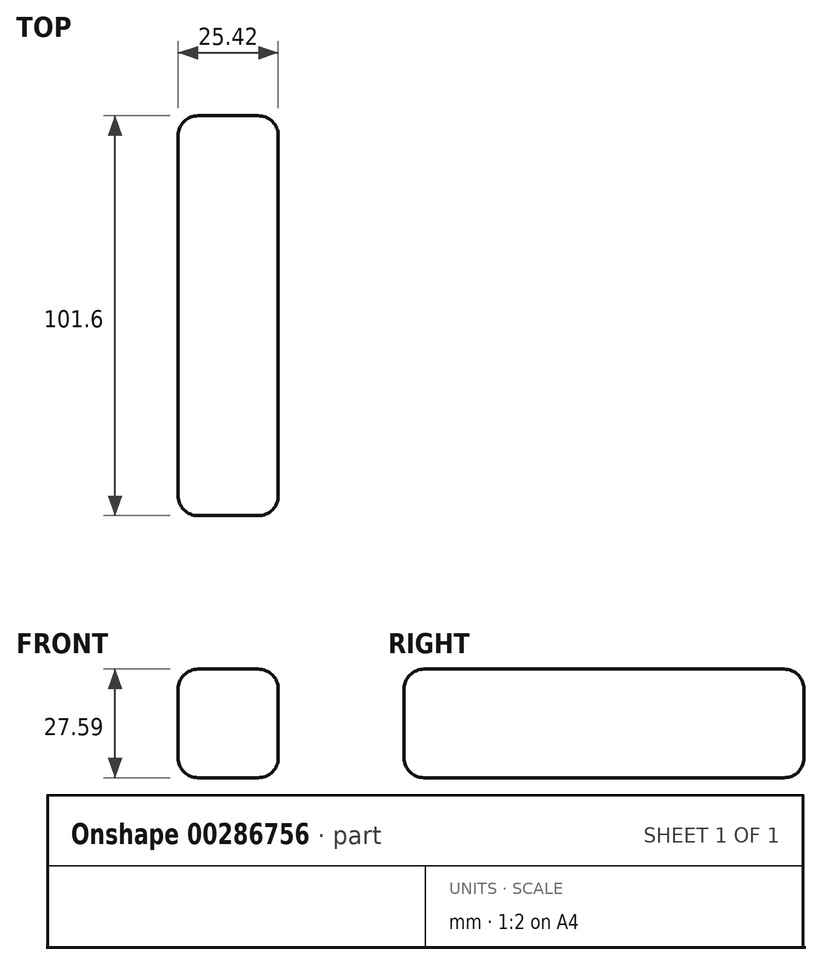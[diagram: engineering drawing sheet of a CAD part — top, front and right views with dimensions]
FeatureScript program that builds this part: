
annotation { "Feature Type Name" : "Feature", "Feature Type Description" : "" }
export const myFeature = defineFeature(function(context is Context, id is Id, definition is map)
    precondition{}
    {
        {
            var Q0;
            Q0=qCreatedBy(makeId("Front.planeOp"),FACE);
            var sketch = newSketch(context, id + "F0", { "sketchPlane" : qUnion([Q0])});
            skLineSegment(sketch, "E0.bottom", {"start": v(-37.05, 48.87) * mm, "end": v(-11.63, 48.87) * mm});
            skLineSegment(sketch, "E0.top", {"start": v(-37.05, 21.28) * mm, "end": v(-11.63, 21.28) * mm});
            skLineSegment(sketch, "E0.left", {"start": v(-37.05, 48.87) * mm, "end": v(-37.05, 21.28) * mm});
            skLineSegment(sketch, "E0.right", {"start": v(-11.63, 48.87) * mm, "end": v(-11.63, 21.28) * mm});
            skSolve(sketch);
        }
        {
            var Q0;
            Q0=makeQuery(id+"F0.imprint","IMPRINT",FACE,{"disambiguationData":[TD([[makeQuery(id+"F0.imprint","IMPRINT",EDGE,{"derivedFrom":sQuery(id+"F0.wireOp",EDGE,"E0.bottom")}),-1.0]])]});
            extrude(context, id + "F1", {"entities" : qUnion([Q0]), "depth" : 101.6 * mm});
        }
        {
            var Q0;
            Q0=makeQuery(id+"F1.opExtrude","SWEPT_EDGE",EDGE,{"disambiguationData":[OSD([sQuery(id+"F0.wireOp",EDGE,"E0.top"),sQuery(id+"F0.wireOp",EDGE,"E0.left")])]});
            var Q1;
            Q1=makeQuery(id+"F1.opExtrude","SWEPT_EDGE",EDGE,{"disambiguationData":[OSD([sQuery(id+"F0.wireOp",EDGE,"E0.bottom"),sQuery(id+"F0.wireOp",EDGE,"E0.right")])]});
            var Q2;
            Q2=makeQuery(id+"F1.opExtrude","SWEPT_EDGE",EDGE,{"disambiguationData":[OSD([sQuery(id+"F0.wireOp",EDGE,"E0.bottom"),sQuery(id+"F0.wireOp",EDGE,"E0.left")])]});
            var Q3;
            Q3=makeQuery(id+"F1.opExtrude","CAP_EDGE",EDGE,{"disambiguationData":[OSD([sQuery(id+"F0.wireOp",EDGE,"E0.bottom")])],"isStart":true});
            var Q4;
            Q4=makeQuery(id+"F1.opExtrude","SWEPT_EDGE",EDGE,{"disambiguationData":[OSD([sQuery(id+"F0.wireOp",EDGE,"E0.top"),sQuery(id+"F0.wireOp",EDGE,"E0.right")])]});
            var Q5;
            Q5=makeQuery(id+"F1.opExtrude","CAP_EDGE",EDGE,{"disambiguationData":[OSD([sQuery(id+"F0.wireOp",EDGE,"E0.bottom")])],"isStart":false});
            var Q6;
            Q6=makeQuery(id+"F1.opExtrude","CAP_EDGE",EDGE,{"disambiguationData":[OSD([sQuery(id+"F0.wireOp",EDGE,"E0.top")])],"isStart":true});
            var Q7;
            Q7=makeQuery(id+"F1.opExtrude","CAP_EDGE",EDGE,{"disambiguationData":[OSD([sQuery(id+"F0.wireOp",EDGE,"E0.top")])],"isStart":false});
            var Q8;
            Q8=makeQuery(id+"F1.opExtrude","CAP_EDGE",EDGE,{"disambiguationData":[OSD([sQuery(id+"F0.wireOp",EDGE,"E0.left")])],"isStart":true});
            var Q9;
            Q9=makeQuery(id+"F1.opExtrude","CAP_EDGE",EDGE,{"disambiguationData":[OSD([sQuery(id+"F0.wireOp",EDGE,"E0.left")])],"isStart":false});
            var Q10;
            Q10=makeQuery(id+"F1.opExtrude","CAP_EDGE",EDGE,{"disambiguationData":[OSD([sQuery(id+"F0.wireOp",EDGE,"E0.right")])],"isStart":true});
            var Q11;
            Q11=makeQuery(id+"F1.opExtrude","CAP_EDGE",EDGE,{"disambiguationData":[OSD([sQuery(id+"F0.wireOp",EDGE,"E0.right")])],"isStart":false});
            fillet(context, id + "F2", {"entities" : qUnion([Q0, Q1, Q2, Q3, Q4, Q5, Q6, Q7, Q8, Q9, Q10, Q11]), "radius" : 5.08 * mm, "tangentPropagation" : true, "allowEdgeOverflow" : false});
        }
    });
